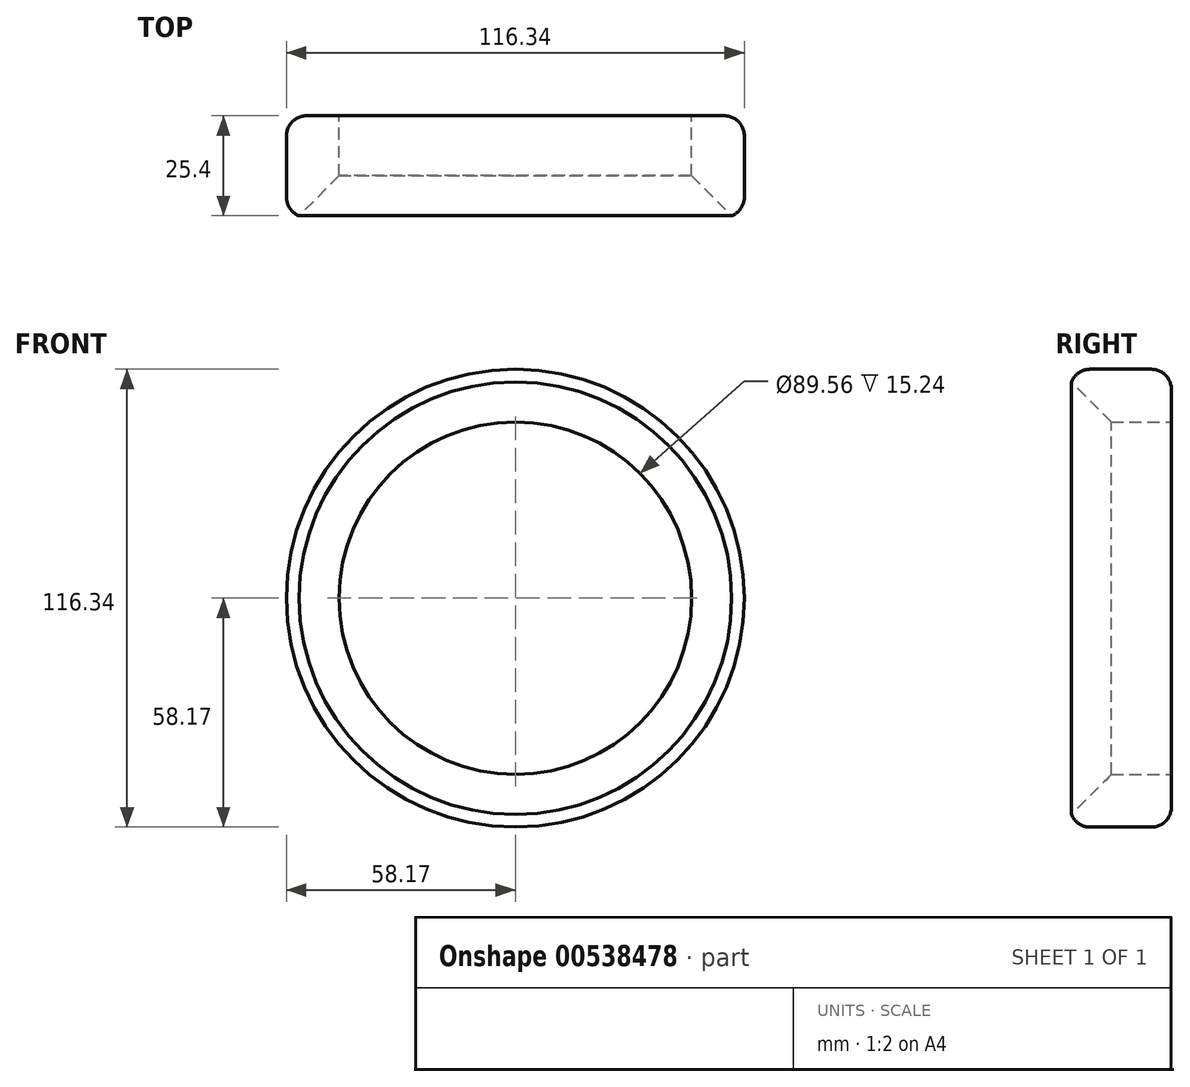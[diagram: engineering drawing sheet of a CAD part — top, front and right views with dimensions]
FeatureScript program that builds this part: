
annotation { "Feature Type Name" : "Feature", "Feature Type Description" : "" }
export const myFeature = defineFeature(function(context is Context, id is Id, definition is map)
    precondition{}
    {
        {
            var Q0;
            Q0=qCreatedBy(makeId("Front.planeOp"),FACE);
            var sketch = newSketch(context, id + "F0", { "sketchPlane" : qUnion([Q0])});
            skCircle(sketch, "E0", {"center": v(0, 0) * mm, "radius": 58.17 * mm});
            skCircle(sketch, "E1", {"center": v(0, 0) * mm, "radius": 44.78 * mm});
            skSolve(sketch);
        }
        {
            var Q0;
            Q0 = qSketchRegion(id + "F0", true);
            extrude(context, id + "F1", {"entities" : qUnion([Q0]), "depth" : 25.4 * mm, "offsetDistance" : 25.4 * mm});
        }
        {
            var Q0;
            Q0=makeQuery(id+"F1.opExtrude","CAP_EDGE",EDGE,{"disambiguationData":[OSD([sQuery(id+"F0.wireOp",EDGE,"E1")])],"isStart":false});
            chamfer(context, id + "F2", {"entities" : qUnion([Q0]), "width" : 10.16 * mm, "tangentPropagation" : true});
        }
        {
            var Q0;
            Q0=makeQuery(id+"F1.opExtrude","CAP_EDGE",EDGE,{"disambiguationData":[OSD([sQuery(id+"F0.wireOp",EDGE,"E0")])],"isStart":false});
            var Q1;
            Q1=makeQuery(id+"F1.opExtrude","CAP_EDGE",EDGE,{"disambiguationData":[OSD([sQuery(id+"F0.wireOp",EDGE,"E0")])],"isStart":true});
            fillet(context, id + "F3", {"entities" : qUnion([Q0, Q1]), "radius" : 5.08 * mm, "tangentPropagation" : true, "allowEdgeOverflow" : false});
        }
    });
